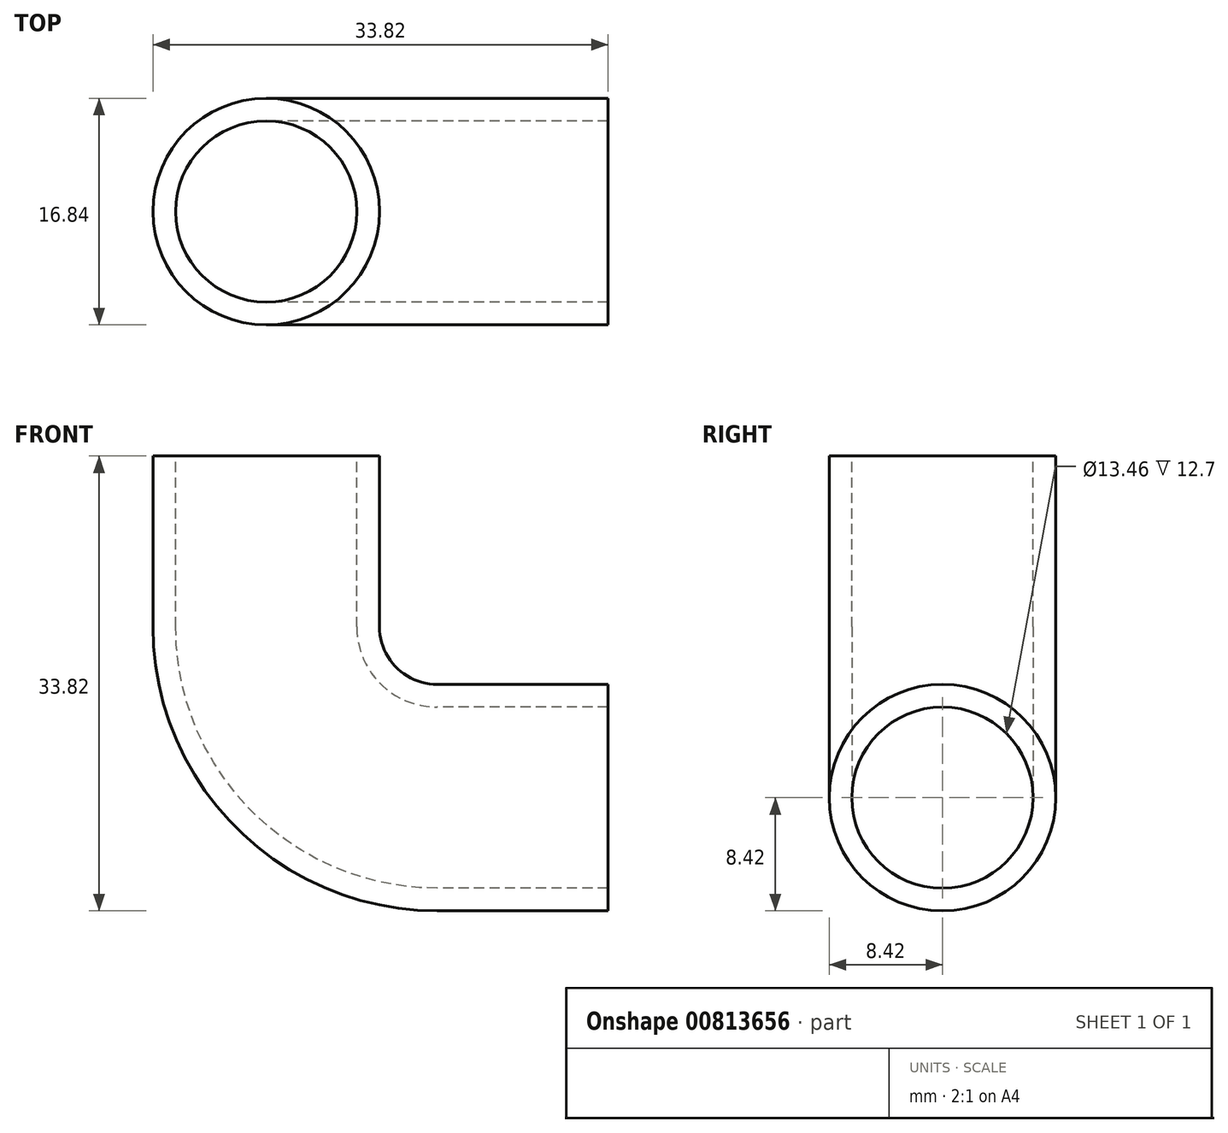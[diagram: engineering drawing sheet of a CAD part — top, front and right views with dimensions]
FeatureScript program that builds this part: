
annotation { "Feature Type Name" : "Feature", "Feature Type Description" : "" }
export const myFeature = defineFeature(function(context is Context, id is Id, definition is map)
    precondition{}
    {
        {
            var Q0;
            Q0=qCreatedBy(makeId("Front.planeOp"),FACE);
            var sketch = newSketch(context, id + "F0", { "sketchPlane" : qUnion([Q0])});
            skLineSegment(sketch, "E0", {"start": v(0, 0) * mm, "end": v(-12.7, 0) * mm});
            skLineSegment(sketch, "E1", {"start": v(-25.4, 12.7) * mm, "end": v(-25.4, 25.4) * mm});
            skPoint(sketch, "E2.visualSharp", {"position": v(-25.4, 0) * mm});
            skArc(sketch, "E2.filletArc", {"start": v(-25.4, 12.7) * mm, "mid": v(-21.68, 3.72) * mm, "end": v(-12.7, 0) * mm});
            skSolve(sketch);
        }
        {
            var Q0;
            Q0=qCreatedBy(makeId("Right.planeOp"),FACE);
            var sketch = newSketch(context, id + "F1", { "sketchPlane" : qUnion([Q0])});
            skCircle(sketch, "E3", {"center": v(0, 0) * mm, "radius": 8.42 * mm});
            skCircle(sketch, "E4", {"center": v(0, 0) * mm, "radius": 6.73 * mm});
            skSolve(sketch);
        }
        {
            var Q0;
            Q0 = qSketchRegion(id + "F1", true);
            var Q1;
            Q1 = qConstructionFilter(qBodyType(qCreatedBy(id + "F0" ,EDGE), BodyType.WIRE), ConstructionObject.NO);
            sweep(context, id + "F2", {"profiles" : qUnion([Q0]), "path" : qUnion([Q1])});
        }
    });
